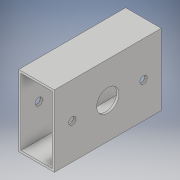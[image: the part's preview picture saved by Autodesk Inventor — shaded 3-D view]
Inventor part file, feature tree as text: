
AUTODESK INVENTOR PART (.ipt)
format: ipt  version: 2018 (Build 220112000, 112)  size: 125,440 bytes
history: native  units: in
note: dims shown in document units (in); Inventor stores cm internally (conversion verified against a paired STEP export)
features: extrude x4, sketch x4
ambient origin geometry x8: Origin, YZ Plane, XZ Plane, XY Plane, X Axis, Y Axis, Z Axis, Center Point
bodies: Solid1 (feature_tree)
feature tree (8):
  extrude  "Extrusion1"  Depth=2.0in
  extrude  "Extrusion2"  Depth=3.0in TaperAngle=0.0deg
  extrude  "Extrusion3"  Depth=0.1875in TaperAngle=0.0deg
  extrude  "Extrusion4"  Depth=2.0in TaperAngle=0.0deg
  sketch  "Sketch1"  dims[d0=1.0in d1=2.0in]
  sketch  "Sketch2"  dims[d2=0.0625in d3=3.0in d4=0.0in]
  sketch  "Sketch3"  dims[d5=0.625in d6=0.1875in d7=0.0in]
  sketch  "Sketch4"  dims[d8=0.5in d9=0.1875in d10=0.0in d11=0.5in d12=2.0in d13=0.2031in d14=2.1875in d15=0.0in]
